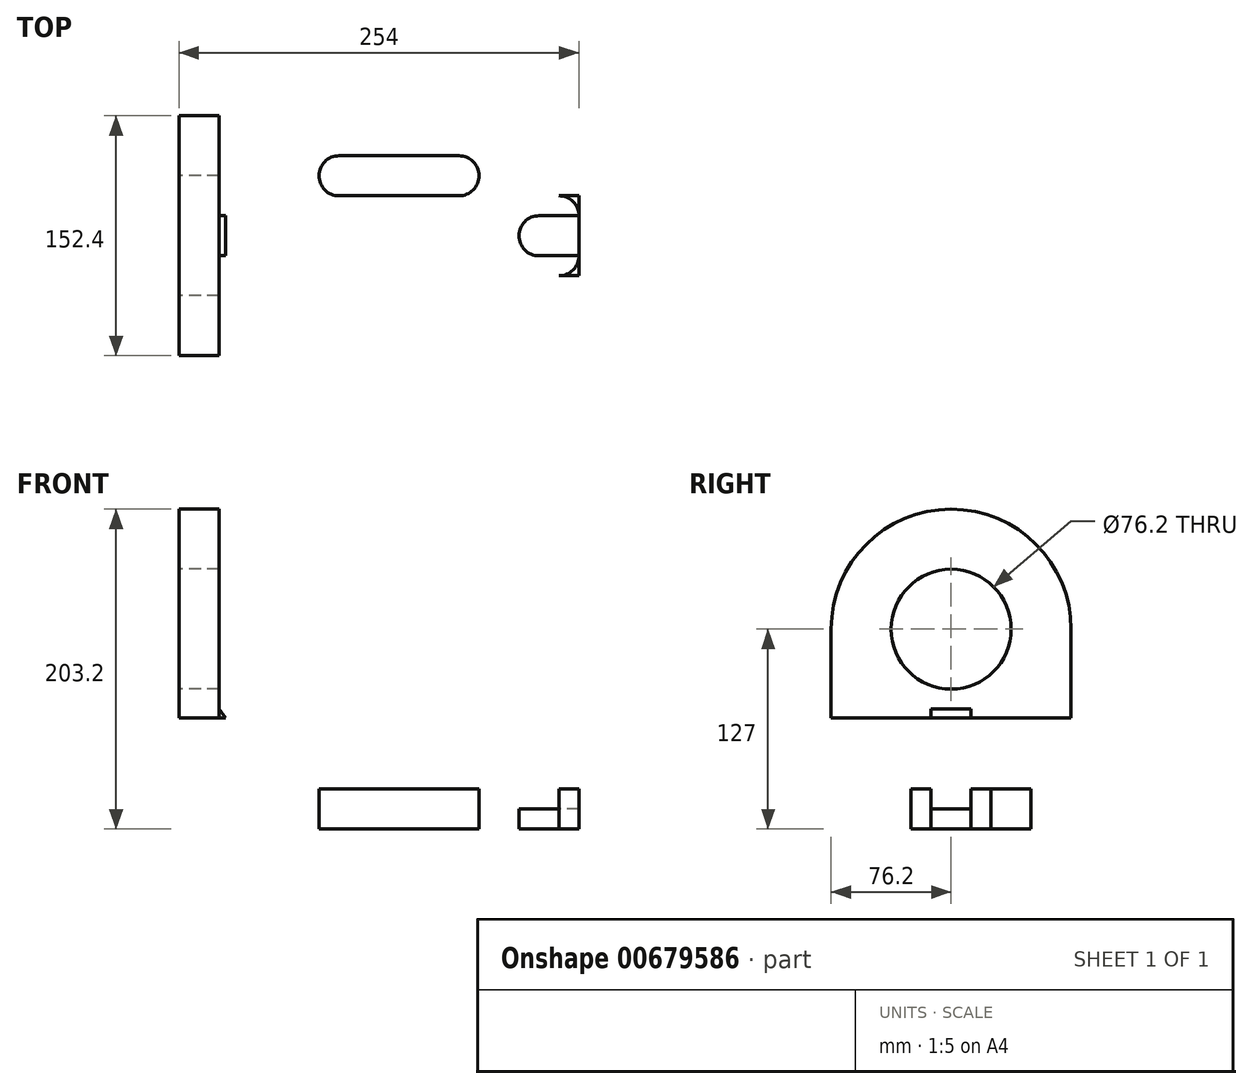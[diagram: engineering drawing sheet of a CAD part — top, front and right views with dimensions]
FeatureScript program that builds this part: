
annotation { "Feature Type Name" : "Feature", "Feature Type Description" : "" }
export const myFeature = defineFeature(function(context is Context, id is Id, definition is map)
    precondition{}
    {
        {
            var Q0;
            Q0=qCreatedBy(makeId("Front.planeOp"),FACE);
            var sketch = newSketch(context, id + "F0", { "sketchPlane" : qUnion([Q0])});
            skLineSegment(sketch, "E0", {"start": v(0, 0) * mm, "end": v(0, 203.2) * mm});
            skLineSegment(sketch, "E1", {"start": v(0, 203.2) * mm, "end": v(25.4, 203.2) * mm});
            skLineSegment(sketch, "E2", {"start": v(254, 25.4) * mm, "end": v(254, 0) * mm});
            skLineSegment(sketch, "E3", {"start": v(254, 0) * mm, "end": v(0, 0) * mm});
            skLineSegment(sketch, "E4", {"start": v(254, 25.4) * mm, "end": v(63.5, 25.4) * mm});
            skLineSegment(sketch, "E5", {"start": v(63.5, 25.4) * mm, "end": v(25.4, 25.4) * mm});
            skLineSegment(sketch, "E6", {"start": v(25.4, 25.4) * mm, "end": v(25.4, 76.2) * mm});
            skLineSegment(sketch, "E7", {"start": v(25.4, 76.2) * mm, "end": v(25.4, 203.2) * mm});
            skLineSegment(sketch, "E8", {"start": v(25.4, 76.2) * mm, "end": v(63.5, 25.4) * mm});
            skSolve(sketch);
        }
        {
            var Q0;
            Q0=makeQuery(id+"F0.imprint","IMPRINT",FACE,{"disambiguationData":[TD([[makeQuery(id+"F0.imprint","IMPRINT",EDGE,{"derivedFrom":sQuery(id+"F0.wireOp",EDGE,"E0")}),-1.0]])]});
            extrude(context, id + "F1", {"entities" : qUnion([Q0]), "endBound" : BoundingType.SYMMETRIC, "depth" : 152.4 * mm, "offsetDistance" : 25.4 * mm});
        }
        {
            var Q0;
            Q0=makeQuery(id+"F0.imprint","IMPRINT",FACE,{"disambiguationData":[TD([[makeQuery(id+"F0.imprint","IMPRINT",EDGE,{"derivedFrom":sQuery(id+"F0.wireOp",EDGE,"E5")}),-1.0]])]});
            extrude(context, id + "F2", {"entities" : qUnion([Q0]), "operationType" : NewBodyOperationType.ADD, "endBound" : BoundingType.SYMMETRIC, "depth" : 25.4 * mm, "offsetDistance" : 25.4 * mm});
        }
        {
            var Q0;
            Q0=makeQuery(id+"F1.opExtrude","SWEPT_FACE",FACE,{"disambiguationData":[OSD([sQuery(id+"F0.wireOp",EDGE,"E0")])]});
            var sketch = newSketch(context, id + "F3", { "sketchPlane" : qUnion([Q0])});
            skLineSegment(sketch, "E9", {"start": v(-76.2, 0) * mm, "end": v(-76.2, 25.4) * mm});
            skLineSegment(sketch, "E10", {"start": v(-76.2, 25.4) * mm, "end": v(-76.2, 127) * mm});
            skLineSegment(sketch, "E11", {"start": v(0, 203.2) * mm, "end": v(76.2, 203.2) * mm});
            skLineSegment(sketch, "E12", {"start": v(76.2, 203.2) * mm, "end": v(76.2, 25.4) * mm});
            skLineSegment(sketch, "E13", {"start": v(76.2, 25.4) * mm, "end": v(76.2, 0) * mm});
            skLineSegment(sketch, "E14", {"start": v(76.2, 0) * mm, "end": v(0, 0) * mm});
            skLineSegment(sketch, "E15", {"start": v(0, 0) * mm, "end": v(-76.2, 0) * mm});
            skLineSegment(sketch, "E16", {"start": v(0, 0) * mm, "end": v(0, 127) * mm});
            skCircle(sketch, "E17", {"center": v(0, 127) * mm, "radius": 38.1 * mm});
            skPoint(sketch, "E18.visualSharp", {"position": v(-76.2, 203.2) * mm});
            skArc(sketch, "E18.filletArc", {"start": v(0, 203.2) * mm, "mid": v(-53.88, 180.88) * mm, "end": v(-76.2, 127) * mm});
            skArc(sketch, "E19.MirrorCS", {"start": v(0, 203.2) * mm, "mid": v(53.88, 180.88) * mm, "end": v(76.2, 127) * mm});
            skSolve(sketch);
        }
        {
            var Q0;
            {var subQ0=sQuery(id+"F3.wireOp",EDGE,"E18.filletArc");Q0=makeQuery(id+"F3.imprint","IMPRINT",FACE,{"disambiguationData":[TD([[makeQuery(id+"F3.imprint","IMPRINT",EDGE,{"derivedFrom":subQ0}),-1.0]])]});}
            var Q1;
            {var subQ0=sQuery(id+"F3.wireOp",EDGE,"E11");Q1=makeQuery(id+"F3.imprint","IMPRINT",FACE,{"disambiguationData":[TD([[makeQuery(id+"F3.imprint","IMPRINT",EDGE,{"derivedFrom":subQ0}),1.0]])]});}
            var Q2;
            Q2=makeQuery(id+"F3.imprint","IMPRINT",FACE,{"disambiguationData":[TD([[makeQuery(id+"F3.imprint","IMPRINT",EDGE,{"derivedFrom":sQuery(id+"F3.wireOp",EDGE,"E17")}),1.0]])]});
            extrude(context, id + "F4", {"entities" : qUnion([Q0, Q1, Q2]), "operationType" : NewBodyOperationType.REMOVE, "endBound" : BoundingType.SYMMETRIC, "oppositeDirection" : true, "depth" : 2540 * mm, "offsetDistance" : 25.4 * mm});
        }
        {
            var Q0;
            Q0=makeQuery(id+"F1.opExtrude","SWEPT_FACE",FACE,{"disambiguationData":[OSD([sQuery(id+"F0.wireOp",EDGE,"E3")])]});
            var sketch = newSketch(context, id + "F5", { "sketchPlane" : qUnion([Q0])});
            skLineSegment(sketch, "E20", {"start": v(215.9, 63.5) * mm, "end": v(215.9, 38.1) * mm});
            skLineSegment(sketch, "E21", {"start": v(228.6, 25.4) * mm, "end": v(241.3, 25.4) * mm});
            skLineSegment(sketch, "E22", {"start": v(254, 12.7) * mm, "end": v(254, 0) * mm});
            skLineSegment(sketch, "E23", {"start": v(254, 12.7) * mm, "end": v(228.6, 12.7) * mm});
            skLineSegment(sketch, "E24", {"start": v(215.9, 0) * mm, "end": v(215.9, 0) * mm});
            skLineSegment(sketch, "E25", {"start": v(203.2, 76.2) * mm, "end": v(190.5, 76.2) * mm});
            skLineSegment(sketch, "E26", {"start": v(190.5, 76.2) * mm, "end": v(88.9, 76.2) * mm});
            skLineSegment(sketch, "E27", {"start": v(88.9, 76.2) * mm, "end": v(0, 76.2) * mm});
            skLineSegment(sketch, "E28", {"start": v(0, 76.2) * mm, "end": v(0, 0) * mm});
            skLineSegment(sketch, "E29", {"start": v(88.9, 76.2) * mm, "end": v(88.9, 50.8) * mm});
            skLineSegment(sketch, "E30", {"start": v(88.9, 38.1) * mm, "end": v(88.9, 38.1) * mm});
            skLineSegment(sketch, "E31", {"start": v(101.6, 25.4) * mm, "end": v(177.8, 25.4) * mm});
            skLineSegment(sketch, "E32", {"start": v(190.5, 38.1) * mm, "end": v(190.5, 38.1) * mm});
            skLineSegment(sketch, "E33", {"start": v(177.8, 50.8) * mm, "end": v(101.6, 50.8) * mm});
            skPoint(sketch, "E34.visualSharp", {"position": v(88.9, 50.8) * mm});
            skArc(sketch, "E34.filletArc", {"start": v(101.6, 50.8) * mm, "mid": v(92.62, 47.08) * mm, "end": v(88.9, 38.1) * mm});
            skPoint(sketch, "E35.visualSharp", {"position": v(88.9, 25.4) * mm});
            skArc(sketch, "E35.filletArc", {"start": v(88.9, 38.1) * mm, "mid": v(92.62, 29.12) * mm, "end": v(101.6, 25.4) * mm});
            skPoint(sketch, "E36.visualSharp", {"position": v(190.5, 50.8) * mm});
            skArc(sketch, "E36.filletArc", {"start": v(190.5, 38.1) * mm, "mid": v(186.78, 47.08) * mm, "end": v(177.8, 50.8) * mm});
            skPoint(sketch, "E37.visualSharp", {"position": v(190.5, 25.4) * mm});
            skArc(sketch, "E37.filletArc", {"start": v(177.8, 25.4) * mm, "mid": v(186.78, 29.12) * mm, "end": v(190.5, 38.1) * mm});
            skPoint(sketch, "E38.visualSharp", {"position": v(215.9, 76.2) * mm});
            skArc(sketch, "E38.filletArc", {"start": v(215.9, 63.5) * mm, "mid": v(212.18, 72.48) * mm, "end": v(203.2, 76.2) * mm});
            skPoint(sketch, "E39.visualSharp", {"position": v(215.9, 25.4) * mm});
            skArc(sketch, "E39.filletArc", {"start": v(215.9, 38.1) * mm, "mid": v(219.62, 29.12) * mm, "end": v(228.6, 25.4) * mm});
            skPoint(sketch, "E40.visualSharp", {"position": v(254, 25.4) * mm});
            skArc(sketch, "E40.filletArc", {"start": v(254, 12.7) * mm, "mid": v(250.28, 21.68) * mm, "end": v(241.3, 25.4) * mm});
            skPoint(sketch, "E41.visualSharp", {"position": v(215.9, 12.7) * mm});
            skArc(sketch, "E41.filletArc", {"start": v(228.6, 12.7) * mm, "mid": v(219.62, 8.98) * mm, "end": v(215.9, 0) * mm});
            skPoint(sketch, "E42.MirrorP", {"position": v(88.9, -25.4) * mm});
            skArc(sketch, "E43.MirrorCS", {"start": v(254, -12.7) * mm, "mid": v(250.28, -21.68) * mm, "end": v(241.3, -25.4) * mm});
            skArc(sketch, "E44.MirrorCS", {"start": v(88.9, -38.1) * mm, "mid": v(92.62, -29.12) * mm, "end": v(101.6, -25.4) * mm});
            skPoint(sketch, "E45.MirrorP", {"position": v(190.5, -25.4) * mm});
            skPoint(sketch, "E46.MirrorP", {"position": v(215.9, -76.2) * mm});
            skPoint(sketch, "E47.MirrorP", {"position": v(190.5, -50.8) * mm});
            skArc(sketch, "E48.MirrorCS", {"start": v(101.6, -50.8) * mm, "mid": v(92.62, -47.08) * mm, "end": v(88.9, -38.1) * mm});
            skLineSegment(sketch, "E49.MirrorCS", {"start": v(177.8, -50.8) * mm, "end": v(101.6, -50.8) * mm});
            skLineSegment(sketch, "E50.MirrorCS", {"start": v(101.6, -25.4) * mm, "end": v(177.8, -25.4) * mm});
            skLineSegment(sketch, "E51.MirrorCS", {"start": v(88.9, -76.2) * mm, "end": v(88.9, -50.8) * mm});
            skPoint(sketch, "E52.MirrorP", {"position": v(88.9, -50.8) * mm});
            skLineSegment(sketch, "E53.MirrorCS", {"start": v(88.9, -76.2) * mm, "end": v(0, -76.2) * mm});
            skPoint(sketch, "E54.MirrorP", {"position": v(215.9, -12.7) * mm});
            skLineSegment(sketch, "E55.MirrorCS", {"start": v(190.5, -76.2) * mm, "end": v(88.9, -76.2) * mm});
            skPoint(sketch, "E56.MirrorP", {"position": v(254, -25.4) * mm});
            skArc(sketch, "E57.MirrorCS", {"start": v(190.5, -38.1) * mm, "mid": v(186.78, -47.08) * mm, "end": v(177.8, -50.8) * mm});
            skLineSegment(sketch, "E58.MirrorCS", {"start": v(254, -12.7) * mm, "end": v(254, 0) * mm});
            skLineSegment(sketch, "E59.MirrorCS", {"start": v(215.9, -63.5) * mm, "end": v(215.9, -38.1) * mm});
            skArc(sketch, "E60.MirrorCS", {"start": v(215.9, -38.1) * mm, "mid": v(219.62, -29.12) * mm, "end": v(228.6, -25.4) * mm});
            skArc(sketch, "E61.MirrorCS", {"start": v(215.9, -63.5) * mm, "mid": v(212.18, -72.48) * mm, "end": v(203.2, -76.2) * mm});
            skLineSegment(sketch, "E62.MirrorCS", {"start": v(254, -12.7) * mm, "end": v(228.6, -12.7) * mm});
            skArc(sketch, "E63.MirrorCS", {"start": v(177.8, -25.4) * mm, "mid": v(186.78, -29.12) * mm, "end": v(190.5, -38.1) * mm});
            skArc(sketch, "E64.MirrorCS", {"start": v(228.6, -12.7) * mm, "mid": v(219.62, -8.98) * mm, "end": v(215.9, 0) * mm});
            skLineSegment(sketch, "E65.MirrorCS", {"start": v(228.6, -25.4) * mm, "end": v(241.3, -25.4) * mm});
            skLineSegment(sketch, "E66.MirrorCS", {"start": v(0, -76.2) * mm, "end": v(0, 0) * mm});
            skLineSegment(sketch, "E67.MirrorCS", {"start": v(203.2, -76.2) * mm, "end": v(190.5, -76.2) * mm});
            skPoint(sketch, "E68.MirrorP", {"position": v(215.9, -25.4) * mm});
            skLineSegment(sketch, "E69", {"start": v(241.3, 25.4) * mm, "end": v(254, 25.4) * mm});
            skLineSegment(sketch, "E70", {"start": v(241.3, -25.4) * mm, "end": v(254, -25.4) * mm});
            skSolve(sketch);
        }
        {
            var Q0;
            Q0=makeQuery(id+"F5.imprint","IMPRINT",FACE,{"disambiguationData":[TD([[makeQuery(id+"F5.imprint","IMPRINT",EDGE,{"derivedFrom":sQuery(id+"F5.wireOp",EDGE,"E20")}),1.0]])]});
            var Q1;
            Q1=makeQuery(id+"F5.imprint","IMPRINT",FACE,{"disambiguationData":[TD([[makeQuery(id+"F5.imprint","IMPRINT",EDGE,{"derivedFrom":sQuery(id+"F5.wireOp",EDGE,"E31")}),1.0]])]});
            var Q2;
            Q2=makeQuery(id+"F5.imprint","IMPRINT",FACE,{"disambiguationData":[TD([[makeQuery(id+"F5.imprint","IMPRINT",EDGE,{"derivedFrom":sQuery(id+"F5.wireOp",EDGE,"E44.MirrorCS")}),-1.0]])]});
            var Q3;
            Q3=makeQuery(id+"F5.imprint","IMPRINT",FACE,{"disambiguationData":[TD([[makeQuery(id+"F5.imprint","IMPRINT",EDGE,{"derivedFrom":sQuery(id+"F5.wireOp",EDGE,"E59.MirrorCS")}),-1.0]])]});
            extrude(context, id + "F6", {"entities" : qUnion([Q0, Q1, Q2, Q3]), "operationType" : NewBodyOperationType.REMOVE, "oppositeDirection" : true, "depth" : 70.61 * mm, "offsetDistance" : 25.4 * mm});
        }
        {
            var Q0;
            Q0=makeQuery(id+"F5.imprint","IMPRINT",FACE,{"disambiguationData":[TD([[makeQuery(id+"F5.imprint","IMPRINT",EDGE,{"derivedFrom":sQuery(id+"F5.wireOp",EDGE,"E22")}),-1.0]])]});
            extrude(context, id + "F7", {"entities" : qUnion([Q0]), "operationType" : NewBodyOperationType.REMOVE, "oppositeDirection" : true, "depth" : 56.13 * mm, "offsetDistance" : 25.4 * mm, "hasSecondDirection" : true, "secondDirectionOppositeDirection" : true, "secondDirectionDepth" : 12.7 * mm});
        }
    });
